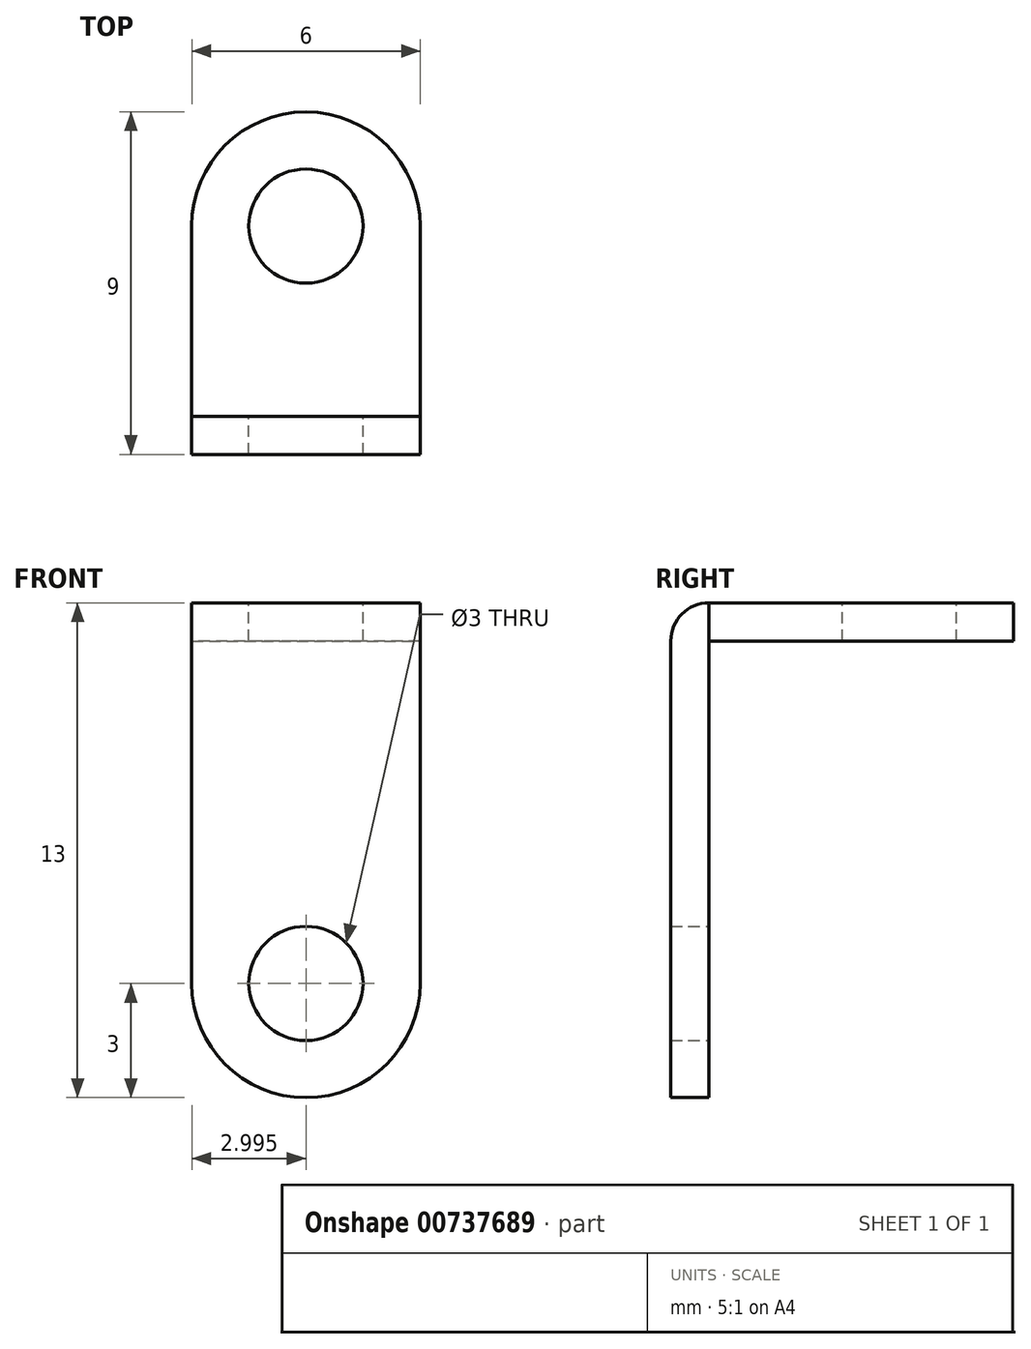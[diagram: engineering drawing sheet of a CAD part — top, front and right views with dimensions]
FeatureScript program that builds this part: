
annotation { "Feature Type Name" : "Feature", "Feature Type Description" : "" }
export const myFeature = defineFeature(function(context is Context, id is Id, definition is map)
    precondition{}
    {
        {
            var Q0;
            Q0=qCreatedBy(makeId("Front.planeOp"),FACE);
            var sketch = newSketch(context, id + "F0", { "sketchPlane" : qUnion([Q0])});
            skLineSegment(sketch, "E0", {"start": v(-0.34, 3) * mm, "end": v(-0.34, 13) * mm});
            skLineSegment(sketch, "E1", {"start": v(-0.34, 13) * mm, "end": v(5.66, 13) * mm});
            skLineSegment(sketch, "E2", {"start": v(5.66, 13) * mm, "end": v(5.66, 3) * mm});
            skLineSegment(sketch, "E3", {"start": v(2.66, 0) * mm, "end": v(2.66, 0) * mm});
            skPoint(sketch, "E4.visualSharp", {"position": v(-0.34, 0) * mm});
            skArc(sketch, "E4.filletArc", {"start": v(-0.34, 3) * mm, "mid": v(0.53, 0.88) * mm, "end": v(2.66, 0) * mm});
            skPoint(sketch, "E5.visualSharp", {"position": v(5.66, 0) * mm});
            skArc(sketch, "E5.filletArc", {"start": v(2.66, 0) * mm, "mid": v(4.78, 0.88) * mm, "end": v(5.66, 3) * mm});
            skCircle(sketch, "E6", {"center": v(2.66, 3) * mm, "radius": 1.5 * mm});
            skSolve(sketch);
        }
        {
            var Q0;
            Q0=makeQuery(id+"F0.imprint","IMPRINT",FACE,{"disambiguationData":[TD([[makeQuery(id+"F0.imprint","IMPRINT",EDGE,{"derivedFrom":sQuery(id+"F0.wireOp",EDGE,"E0")}),-1.0]])]});
            extrude(context, id + "F1", {"entities" : qUnion([Q0]), "depth" : 1 * mm, "offsetDistance" : 25 * mm});
        }
        {
            var Q0;
            Q0=makeQuery(id+"F1.opExtrude","SWEPT_FACE",FACE,{"disambiguationData":[OSD([sQuery(id+"F0.wireOp",EDGE,"E1")])]});
            var sketch = newSketch(context, id + "F2", { "sketchPlane" : qUnion([Q0])});
            skLineSegment(sketch, "E7.0", {"start": v(-0.34, 0) * mm, "end": v(5.66, 0) * mm});
            skLineSegment(sketch, "E8", {"start": v(-0.34, 0) * mm, "end": v(-0.34, 5) * mm});
            skLineSegment(sketch, "E9", {"start": v(5.66, 0) * mm, "end": v(5.66, 5) * mm});
            skArc(sketch, "E10", {"start": v(5.66, 5) * mm, "mid": v(2.66, 8) * mm, "end": v(-0.34, 5) * mm});
            skCircle(sketch, "E11", {"center": v(2.66, 5) * mm, "radius": 1.5 * mm});
            skSolve(sketch);
        }
        {
            var Q0;
            Q0=makeQuery(id+"F2.imprint","IMPRINT",FACE,{"disambiguationData":[TD([[makeQuery(id+"F2.imprint","IMPRINT",EDGE,{"derivedFrom":sQuery(id+"F2.wireOp",EDGE,"E7.0")}),1.0]])]});
            extrude(context, id + "F3", {"entities" : qUnion([Q0]), "oppositeDirection" : true, "depth" : 1 * mm, "offsetDistance" : 25 * mm});
        }
        {
            var Q0;
            Q0=makeQuery(id+"F1.opExtrude","CAP_EDGE",EDGE,{"disambiguationData":[OSD([sQuery(id+"F0.wireOp",EDGE,"E1")])],"isStart":false});
            fillet(context, id + "F4", {"entities" : qUnion([Q0]), "radius" : 1 * mm, "tangentPropagation" : true, "allowEdgeOverflow" : false});
        }
    });
